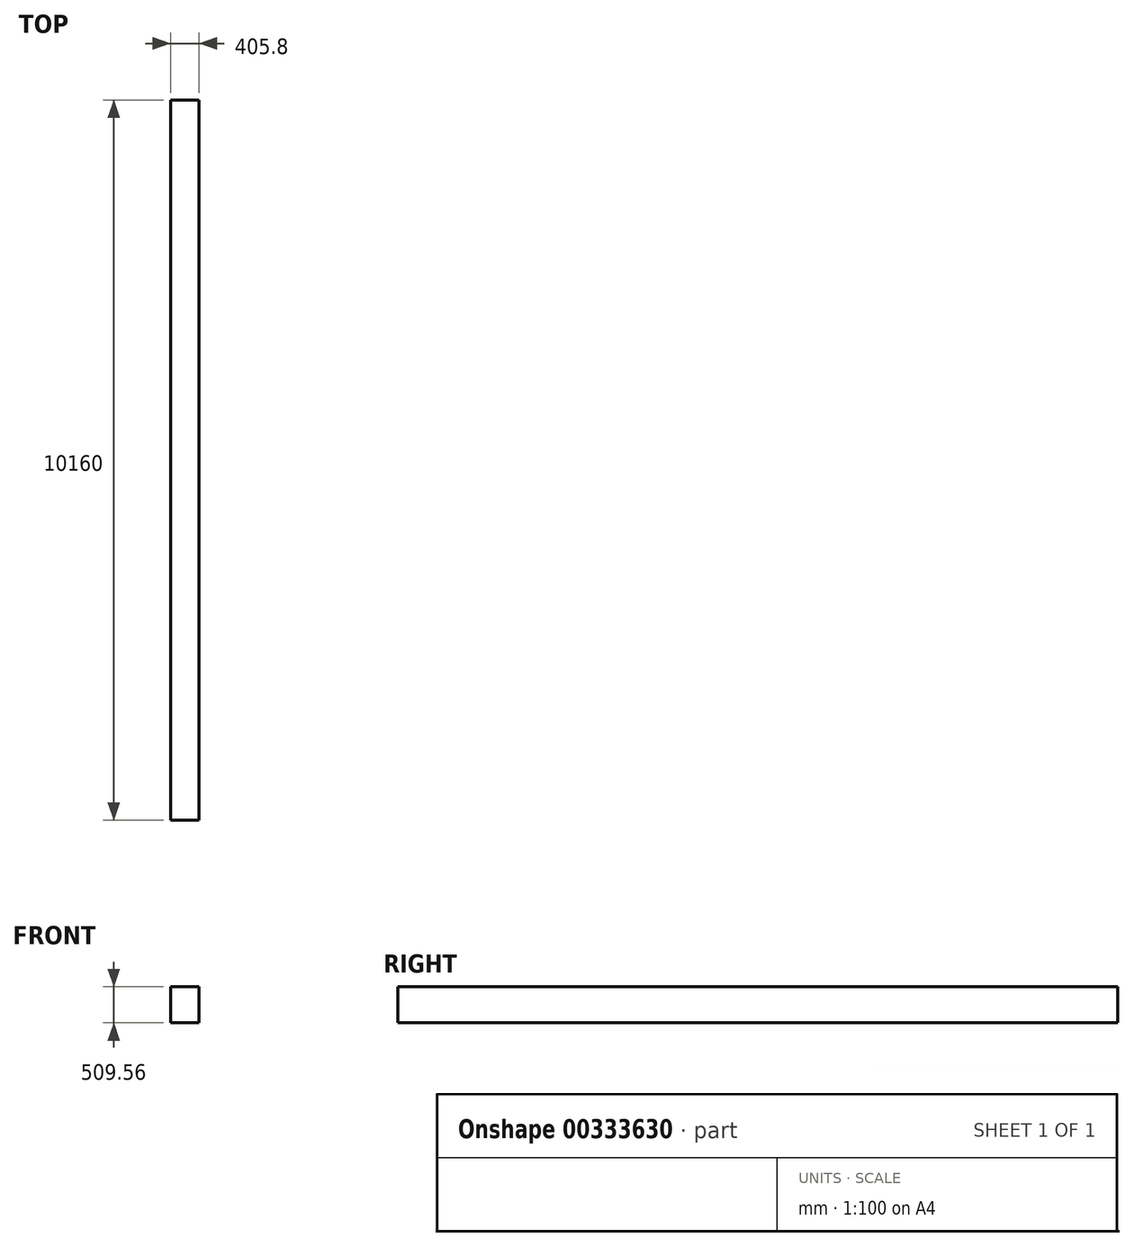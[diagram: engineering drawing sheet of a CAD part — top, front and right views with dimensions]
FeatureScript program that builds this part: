
annotation { "Feature Type Name" : "Feature", "Feature Type Description" : "" }
export const myFeature = defineFeature(function(context is Context, id is Id, definition is map)
    precondition{}
    {
        {
            var Q0;
            Q0=qCreatedBy(makeId("Front.planeOp"),FACE);
            var sketch = newSketch(context, id + "F0", { "sketchPlane" : qUnion([Q0])});
            skLineSegment(sketch, "E0.bottom", {"start": v(-582.66, -83.6) * mm, "end": v(-176.86, -83.6) * mm});
            skLineSegment(sketch, "E0.top", {"start": v(-582.66, 425.96) * mm, "end": v(-176.86, 425.96) * mm});
            skLineSegment(sketch, "E0.left", {"start": v(-582.66, -83.6) * mm, "end": v(-582.66, 425.96) * mm});
            skLineSegment(sketch, "E0.right", {"start": v(-176.86, -83.6) * mm, "end": v(-176.86, 425.96) * mm});
            skSolve(sketch);
        }
        {
            var Q0;
            Q0 = qSketchRegion(id + "F0", true);
            extrude(context, id + "F1", {"entities" : qUnion([Q0]), "depth" : 10160 * mm});
        }
    });
